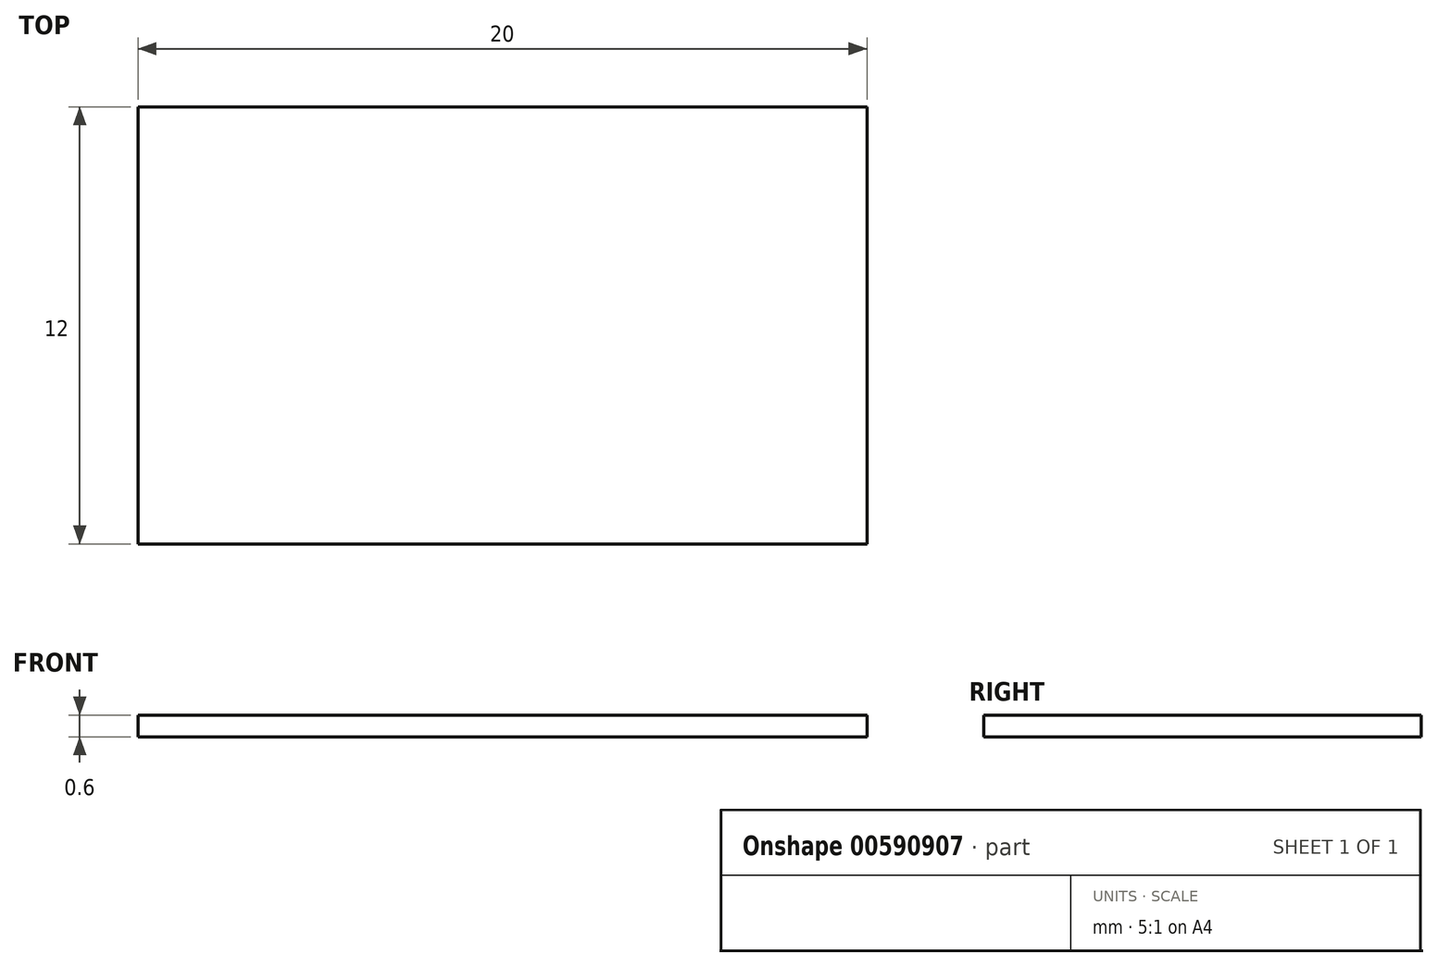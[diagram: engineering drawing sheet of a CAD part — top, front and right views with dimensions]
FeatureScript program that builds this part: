
annotation { "Feature Type Name" : "Feature", "Feature Type Description" : "" }
export const myFeature = defineFeature(function(context is Context, id is Id, definition is map)
    precondition{}
    {
        {
            var Q0;
            Q0=qCreatedBy(makeId("Top.planeOp"),FACE);
            var sketch = newSketch(context, id + "F0", { "sketchPlane" : qUnion([Q0])});
            skLineSegment(sketch, "E0.bottom", {"start": v(-10, 6) * mm, "end": v(10, 6) * mm});
            skLineSegment(sketch, "E0.top", {"start": v(-10, -6) * mm, "end": v(10, -6) * mm});
            skLineSegment(sketch, "E0.left", {"start": v(-10, 6) * mm, "end": v(-10, -6) * mm});
            skLineSegment(sketch, "E0.right", {"start": v(10, 6) * mm, "end": v(10, -6) * mm});
            skPoint(sketch, "E0.middle", {"position": v(0, 0) * mm});
            skLineSegment(sketch, "E1.bottom", {"start": v(1, 5) * mm, "end": v(-9, 5) * mm});
            skLineSegment(sketch, "E1.top", {"start": v(1, -5) * mm, "end": v(-9, -5) * mm});
            skLineSegment(sketch, "E1.left", {"start": v(1, 5) * mm, "end": v(1, -5) * mm});
            skLineSegment(sketch, "E1.right", {"start": v(-9, 5) * mm, "end": v(-9, -5) * mm});
            skPoint(sketch, "E1.middle", {"position": v(-4, 0) * mm});
            skSolve(sketch);
        }
        {
            var Q0;
            Q0=makeQuery(id+"F0.imprint","IMPRINT",FACE,{"disambiguationData":[TD([[makeQuery(id+"F0.imprint","IMPRINT",EDGE,{"derivedFrom":sQuery(id+"F0.wireOp",EDGE,"E0.bottom")}),-1.0]])]});
            var Q1;
            Q1=makeQuery(id+"F0.imprint","IMPRINT",FACE,{"disambiguationData":[TD([[makeQuery(id+"F0.imprint","IMPRINT",EDGE,{"derivedFrom":sQuery(id+"F0.wireOp",EDGE,"E1.bottom")}),1.0]])]});
            extrude(context, id + "F1", {"entities" : qUnion([Q0, Q1]), "depth" : 0.6 * mm, "offsetDistance" : 25 * mm});
        }
    });
